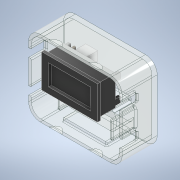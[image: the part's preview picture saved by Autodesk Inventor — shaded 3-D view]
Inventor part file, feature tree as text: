
AUTODESK INVENTOR PART (.ipt)
format: ipt  version: 2022 (Build 260153000, 153)  size: 788,480 bytes
history: native  units: in
note: dims shown in document units (in); Inventor stores cm internally (conversion verified against a paired STEP export)
features: extrude x18, sketch x18, fillet x6, other x4, plane x1
ambient origin geometry x8: Origin, YZ Plane, XZ Plane, XY Plane, X Axis, Y Axis, Z Axis, Center Point
bodies: Body1 (feature_tree), Body2 (feature_tree), Body3 (feature_tree), Body4 (feature_tree)
feature tree (47):
  other  "Faceplate"
  extrude  "Front Panel Blank"  Depth=2.5591in
  extrude  "Voltmeter Screen"  Depth=1.5748in
  extrude  "Extrusion45"  Depth=0.3937in TaperAngle=0.0deg
  extrude  "Extrusion46"  Depth=0.5906in
  extrude  "Extrusion47"  Depth=0.0197in
  extrude  "Extrusion48"  Depth=0.0197in
  extrude  "Extrusion49"  Depth=1.0236in
  extrude  "Extrusion50"  Depth=0.3937in
  fillet  "Fillet36"  Radius=0.1969in
  fillet  "Fillet37"  Radius=0.3937in
  extrude  "Extrusion51"  Depth=0.0906in
  extrude  "Extrusion52"  Depth=0.0787in
  extrude  "Extrusion53"  Depth=0.0295in
  plane  "Work Plane2"
  extrude  "PSU PCB"  Depth=0.0551in
  extrude  "Extrusion55"  Depth=0.2323in
  extrude  "Extrusion56"  Depth=0.2087in
  extrude  "Extrusion57"  Depth=0.0984in TaperAngle=0.0deg
  extrude  "Extrusion58"  Depth=0.3937in
  extrude  "Extrusion59"  Depth=0.3937in
  fillet  "Fillet38"  Radius=0.0079in
  fillet  "Fillet39"  Radius=0.5748in
  fillet  "Fillet40"  Radius=0.0591in
  fillet  "Fillet41"  Radius=0.0591in
  extrude  "Extrusion60"  Depth=0.3937in
  sketch  "Sketch1"  dims[d0=3.1496in d1=2.5591in]
  sketch  "Sketch3"  dims[d2=1.2795in d4=1.5748in]
  sketch  "Sketch59"  dims[d5=0.3937in d6=0.0984in d7=0.0in]
  other  "Screen"
  sketch  "Sketch60"  dims[d30=1.7717in d31=0.5906in d32=1.0236in d33=0.8858in]
  sketch  "Sketch61"  dims[d34=0.9449in d35=0.4724in d36=0.0197in d37=0.0197in]
  sketch  "Sketch64"  dims[d38=0.0197in d39=0.0197in]
  sketch  "Sketch65"  dims[d40=0.9449in d43=1.0236in]
  sketch  "Sketch66"  dims[d44=0.4724in d45=1.063in d46=0.1969in d47=0.0in d85=0.3937in]
  sketch  "Sketch67"  dims[d161=0.315in d270=0.0906in]
  sketch  "Sketch68"  dims[d377=1.1024in d380=0.7283in d381=0.0787in d386=0.0394in]
  sketch  "Sketch70"  dims[d481=0.0in d488=0.0in d489=0.0in d491=0.1772in d492=0.1772in]
  other  "Box"
  sketch  "Sketch71"  dims[d688=0.0394in d689=0.2953in d690=0.0394in d691=0.1181in d701=0.1732in d702=0.1772in d704=0.0787in d705=0.0787in d811=1.8819in]
  other  "PSU"
  sketch  "Sketch72"  dims[d812=1.122in d814=0.0295in]
  sketch  "Sketch73"  dims[d815=0.0295in d816=0.0551in]
  sketch  "Sketch74"  dims[d817=0.0551in d819=0.2323in]
  sketch  "Sketch75"  dims[d820=0.2323in d821=0.2087in]
  sketch  "Sketch76"  dims[d822=0.2087in d823=0.0984in d824=0.0in]
  sketch  "Sketch77"  dims[d825=0.0079in d826=0.0079in d827=0.0079in d828=0.0079in d829=0.5748in d830=0.0in d831=0.0591in d832=0.0591in d833=0.25in d834=0.25in d835=0.0831in d836=0.0831in d837=0.1669in d838=0.0in d839=0.4024in d840=0.3165in d841=0.2756in d842=0.1181in d843=0.4724in d844=0.0in d845=0.3937in d846=0.2205in d847=0.4921in d848=0.3386in d849=0.2008in d850=0.0in d851=0.4764in d852=0.0846in d853=0.1969in d854=0.5906in d855=0.248in d856=0.0in d857=0.0413in d858=0.0394in d859=0.4331in d860=0.4331in d862=0.4331in d863=0.4331in d864=0.1575in d865=0.1575in d866=0.1575in d867=0.1575in d868=0.0984in d869=0.0984in d870=0.0984in d871=0.0984in d872=0.1181in d873=0.0in d874=0.3937in d875=0.315in d876=1.1024in d877=0.0in d881=0.3937in d882=0.0787in d883=0.0in d884=0.8386in d885=1.7126in d886=0.6201in d887=0.6201in d888=0.1181in d889=0.3508in d890=0.0in d891=0.089in d892=0.0638in d893=0.726in d894=0.1614in d895=0.0in d896=0.1181in d897=0.1181in d898=0.1181in d899=0.1181in d900=0.1181in d901=0.0787in d902=0.0787in d903=0.0787in d904=0.7874in d905=0.0in d906=0.2362in d907=0.2362in d908=0.0in d910=0.315in d911=0.0in d912=0.0in d913=0.0in d914=0.1969in d915=0.1181in d916=0.1181in d917=0.1181in d918=0.1181in d919=0.1969in d920=0.5906in d921=0.0in d922=0.6201in d923=0.6201in d924=0.1181in d925=0.8386in d926=0.5906in d927=0.0394in d928=0.0394in d929=0.5906in d930=0.2756in d931=0.5906in d932=0.2756in d933=0.0394in d934=0.0394in d935=0.5118in d936=0.0in d937=0.0394in d938=0.0394in d939=0.0394in d940=0.0394in d941=0.9055in d942=0.9055in d943=0.9055in d944=0.9055in d945=0.3937in d951=0.9055in d952=0.9055in d953=0.3937in d954=0.5118in d955=-0.0687in]
